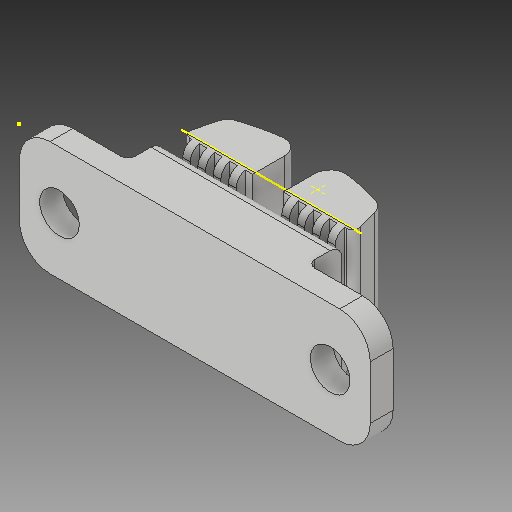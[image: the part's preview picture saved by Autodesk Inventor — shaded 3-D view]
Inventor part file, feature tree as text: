
AUTODESK INVENTOR PART (.ipt)
format: ipt  version: 2017 (Build 210142000, 142)  size: 300,032 bytes
history: native  units: mm
features: sketch x13, other x3
ambient origin geometry x8: Origin, YZ Plane, XZ Plane, XY Plane, X Axis, Y Axis, Z Axis, Center Point
bodies: Solid1 (feature_tree)
feature tree (16):
  other  "X Belt Clamp.ipt"
  other  "Solid1::X Belt Clamp.ipt"
  other  "TaggingFeature1"
  sketch  "Sketch1"  dims[d0=10.0mm]
  sketch  "Sketch2"
  sketch  "Sketch3"
  sketch  "Sketch4"
  sketch  "Sketch5"
  sketch  "Sketch6"
  sketch  "Sketch7"
  sketch  "Sketch8"
  sketch  "Sketch9"
  sketch  "Sketch10"
  sketch  "Sketch11"
  sketch  "Sketch12"
  sketch  "Sketch13"
